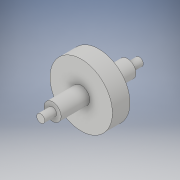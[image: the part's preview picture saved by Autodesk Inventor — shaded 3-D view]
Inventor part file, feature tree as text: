
AUTODESK INVENTOR PART (.ipt)
format: ipt  version: 2018 (Build 220112000, 112)  size: 124,928 bytes
history: native  units: in
note: dims shown in document units (in); Inventor stores cm internally (conversion verified against a paired STEP export)
features: sketch x6, extrude x5
ambient origin geometry x8: Origin, YZ Plane, XZ Plane, XY Plane, X Axis, Y Axis, Z Axis, Center Point
bodies: Solid1 (feature_tree)
feature tree (11):
  extrude  "Extrusion1"  Depth=0.078in TaperAngle=0.0deg
  extrude  "Extrusion2"  Depth=0.189in TaperAngle=0.0deg
  extrude  "Extrusion3"  Depth=0.116in TaperAngle=0.0deg
  sketch  "Sketch4"  dims[d9=0.112in d10=0.189in d11=0.0in]
  extrude  "Extrusion4"  Depth=0.189in TaperAngle=0.0deg
  extrude  "Extrusion5"  Depth=0.078in TaperAngle=0.0deg
  sketch  "Sketch1"  dims[d0=0.053in d1=0.078in d2=0.0in]
  sketch  "Sketch2"  dims[d3=0.112in d4=0.189in d5=0.0in]
  sketch  "Sketch3"  dims[d6=0.411in d7=0.116in d8=0.0in]
  sketch  "Sketch5"  dims[d12=0.053in d13=0.078in d14=0.0in]
  sketch  "Sketch6"
